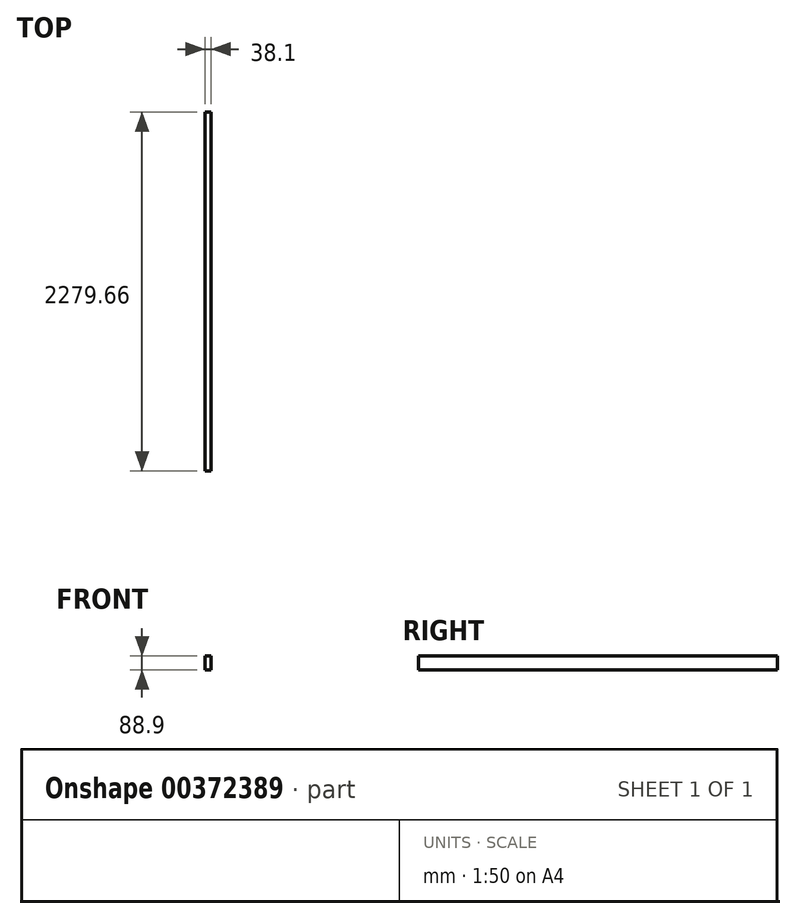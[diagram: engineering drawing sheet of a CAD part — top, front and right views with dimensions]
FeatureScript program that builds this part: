
annotation { "Feature Type Name" : "Feature", "Feature Type Description" : "" }
export const myFeature = defineFeature(function(context is Context, id is Id, definition is map)
    precondition{}
    {
        {
            var Q0;
            Q0=qCreatedBy(makeId("Front.planeOp"),FACE);
            var sketch = newSketch(context, id + "F0", { "sketchPlane" : qUnion([Q0])});
            skLineSegment(sketch, "E0.bottom", {"start": v(-19.05, 44.45) * mm, "end": v(19.05, 44.45) * mm});
            skLineSegment(sketch, "E0.top", {"start": v(-19.05, -44.45) * mm, "end": v(19.05, -44.45) * mm});
            skLineSegment(sketch, "E0.left", {"start": v(-19.05, 44.45) * mm, "end": v(-19.05, -44.45) * mm});
            skLineSegment(sketch, "E0.right", {"start": v(19.05, 44.45) * mm, "end": v(19.05, -44.45) * mm});
            skPoint(sketch, "E0.middle", {"position": v(0, 0) * mm});
            skSolve(sketch);
        }
        {
            var Q0;
            Q0=qSketchRegion(id+"F0",true);
            extrude(context, id + "F1", {"entities" : qUnion([Q0]), "endBound" : BoundingType.SYMMETRIC, "oppositeDirection" : true, "depth" : 2279.65 * mm});
        }
    });
